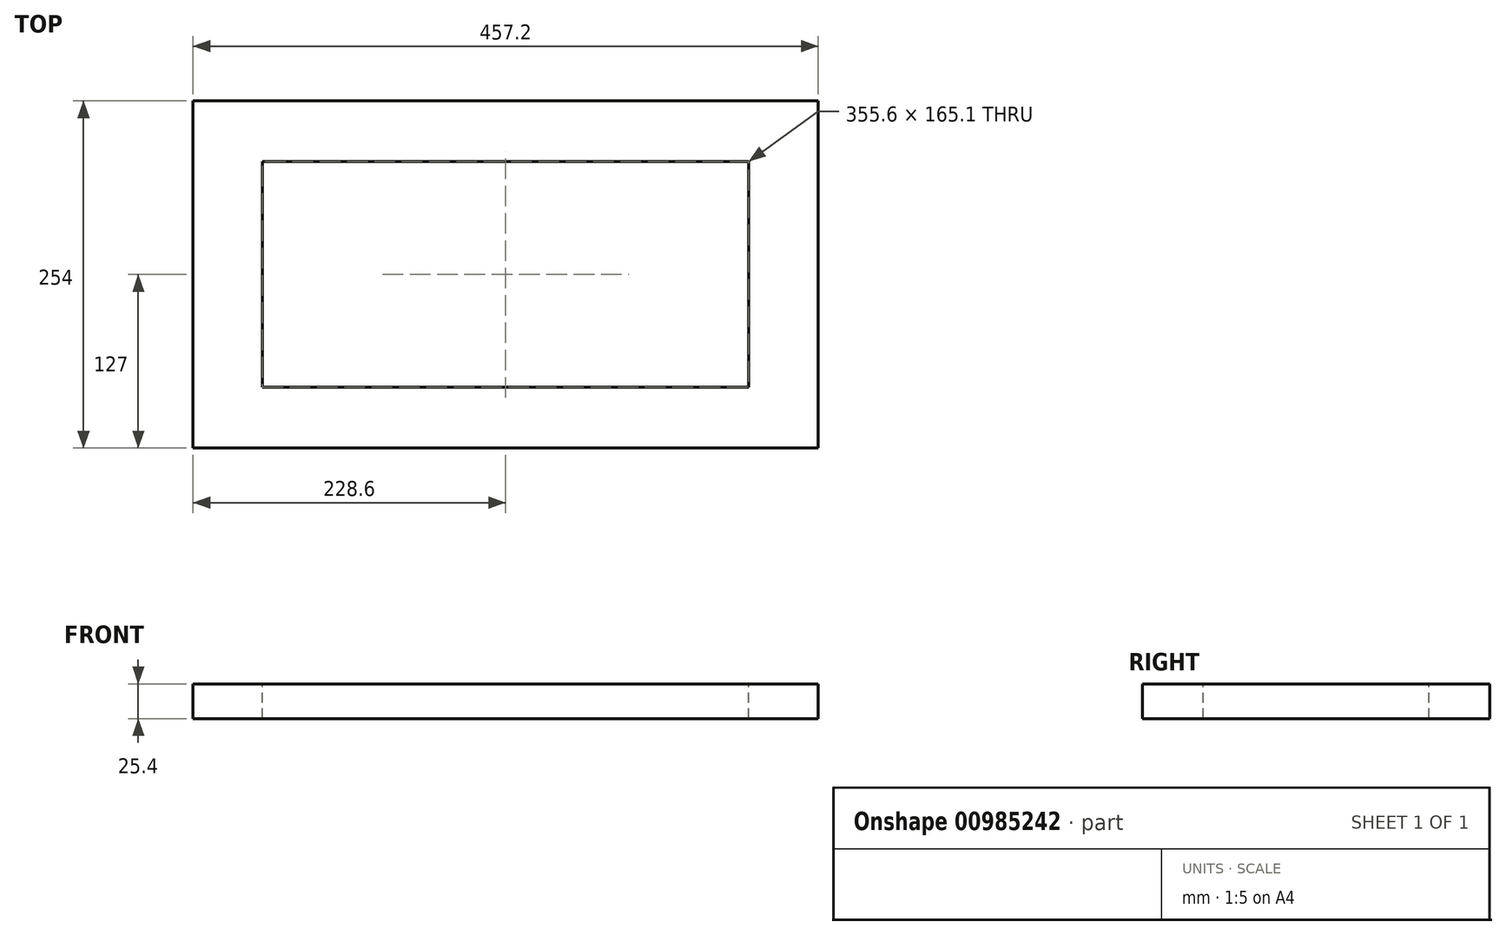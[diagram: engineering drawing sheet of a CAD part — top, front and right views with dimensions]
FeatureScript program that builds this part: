
annotation { "Feature Type Name" : "Feature", "Feature Type Description" : "" }
export const myFeature = defineFeature(function(context is Context, id is Id, definition is map)
    precondition{}
    {
        {
            var Q0;
            Q0=qCreatedBy(makeId("Top.planeOp"),FACE);
            var sketch = newSketch(context, id + "F0", { "sketchPlane" : qUnion([Q0])});
            skLineSegment(sketch, "E0.bottom", {"start": v(0, 0) * mm, "end": v(457.2, 0) * mm});
            skLineSegment(sketch, "E0.top", {"start": v(0, 254) * mm, "end": v(457.2, 254) * mm});
            skLineSegment(sketch, "E0.left", {"start": v(0, 0) * mm, "end": v(0, 254) * mm});
            skLineSegment(sketch, "E0.right", {"start": v(457.2, 0) * mm, "end": v(457.2, 254) * mm});
            skLineSegment(sketch, "E1.bottom", {"start": v(50.8, 209.55) * mm, "end": v(406.4, 209.55) * mm});
            skLineSegment(sketch, "E1.top", {"start": v(50.8, 44.45) * mm, "end": v(406.4, 44.45) * mm});
            skLineSegment(sketch, "E1.left", {"start": v(50.8, 209.55) * mm, "end": v(50.8, 44.45) * mm});
            skLineSegment(sketch, "E1.right", {"start": v(406.4, 209.55) * mm, "end": v(406.4, 44.45) * mm});
            skSolve(sketch);
        }
        {
            var Q0;
            Q0 = qSketchRegion(id + "F0", true);
            extrude(context, id + "F1", {"entities" : qUnion([Q0]), "oppositeDirection" : true, "depth" : 25.4 * mm, "offsetDistance" : 25.4 * mm});
        }
    });
